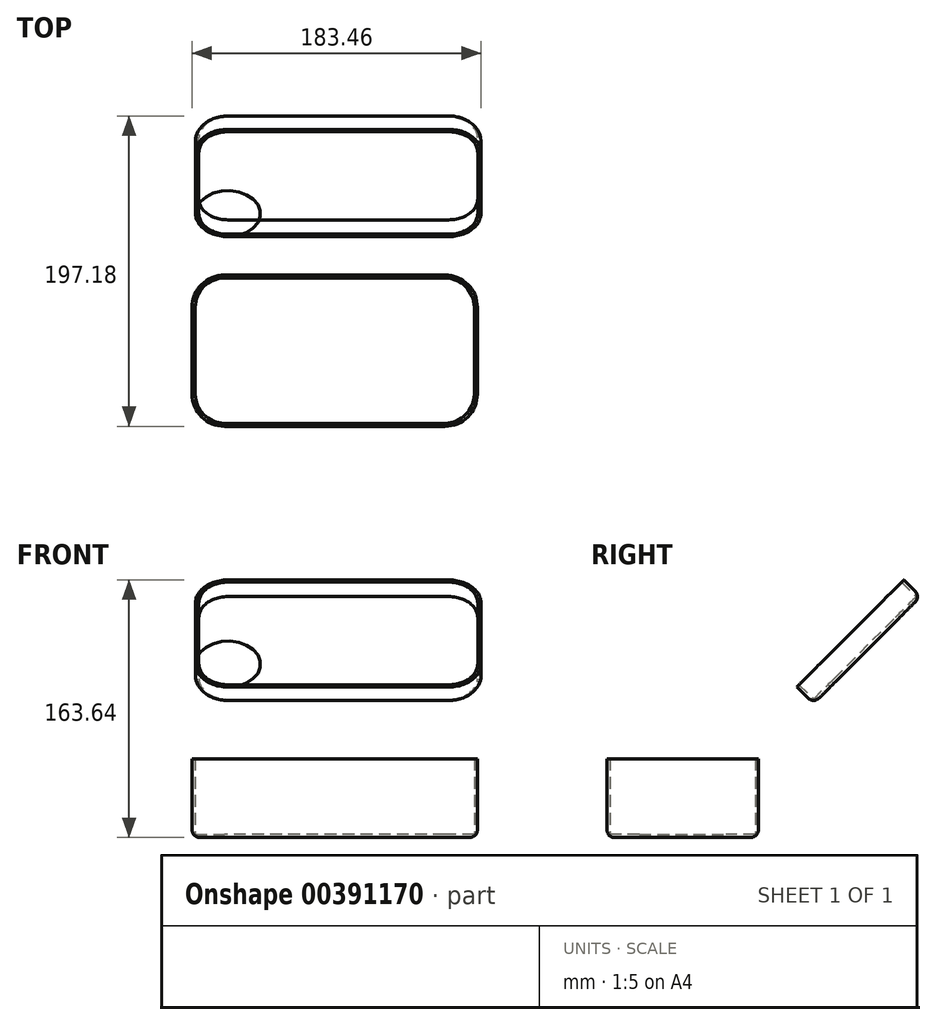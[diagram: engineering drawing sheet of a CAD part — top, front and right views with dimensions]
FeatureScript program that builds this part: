
annotation { "Feature Type Name" : "Feature", "Feature Type Description" : "" }
export const myFeature = defineFeature(function(context is Context, id is Id, definition is map)
    precondition{}
    {
        {
            var Q0;
            Q0=qCreatedBy(makeId("Top.planeOp"),FACE);
            var sketch = newSketch(context, id + "F0", { "sketchPlane" : qUnion([Q0])});
            skPoint(sketch, "E0.middle", {"position": v(0, 0) * mm});
            skLineSegment(sketch, "E1", {"start": v(-70.02, -46.05) * mm, "end": v(69.98, -46.05) * mm});
            skLineSegment(sketch, "E2", {"start": v(-88.63, -27.45) * mm, "end": v(-88.63, 27.55) * mm});
            skLineSegment(sketch, "E3", {"start": v(-90.63, 27.55) * mm, "end": v(-90.63, -27.45) * mm});
            skLineSegment(sketch, "E4", {"start": v(69.98, 46.16) * mm, "end": v(-70.02, 46.16) * mm});
            skLineSegment(sketch, "E5", {"start": v(-70.02, 48.16) * mm, "end": v(69.98, 48.16) * mm});
            skLineSegment(sketch, "E6", {"start": v(69.98, -48.05) * mm, "end": v(-70.02, -48.05) * mm});
            skArc(sketch, "E7", {"start": v(-90.63, 27.55) * mm, "mid": v(-84.6, 42.13) * mm, "end": v(-70.02, 48.16) * mm});
            skArc(sketch, "E8", {"start": v(-88.63, 27.55) * mm, "mid": v(-83.18, 40.71) * mm, "end": v(-70.02, 46.16) * mm});
            skArc(sketch, "E9", {"start": v(-70.02, -46.05) * mm, "mid": v(-83.18, -40.6) * mm, "end": v(-88.63, -27.45) * mm});
            skArc(sketch, "E10", {"start": v(-70.02, -48.05) * mm, "mid": v(-84.6, -42.02) * mm, "end": v(-90.63, -27.45) * mm});
            skLineSegment(sketch, "E11", {"start": v(90.59, 27.55) * mm, "end": v(90.59, -27.45) * mm});
            skArc(sketch, "E12", {"start": v(69.98, -46.05) * mm, "mid": v(83.14, -40.6) * mm, "end": v(88.59, -27.45) * mm});
            skArc(sketch, "E13", {"start": v(69.98, -48.05) * mm, "mid": v(84.55, -42.02) * mm, "end": v(90.59, -27.45) * mm});
            skLineSegment(sketch, "E14", {"start": v(88.59, 27.55) * mm, "end": v(88.59, -27.45) * mm});
            skArc(sketch, "E15", {"start": v(69.98, 46.16) * mm, "mid": v(83.14, 40.71) * mm, "end": v(88.59, 27.55) * mm});
            skArc(sketch, "E16", {"start": v(69.98, 48.16) * mm, "mid": v(84.55, 42.13) * mm, "end": v(90.59, 27.55) * mm});
            skSolve(sketch);
        }
        {
            var Q0;
            Q0=makeQuery(id+"F0.imprint","IMPRINT",FACE,{"disambiguationData":[TD([[makeQuery(id+"F0.imprint","IMPRINT",EDGE,{"derivedFrom":sQuery(id+"F0.wireOp",EDGE,"E1")}),-1.0]])]});
            extrude(context, id + "F1", {"entities" : qUnion([Q0]), "depth" : 50 * mm, "offsetDistance" : 25 * mm});
        }
        {
            var Q0;
            Q0=makeQuery(id+"F0.imprint","IMPRINT",FACE,{"disambiguationData":[TD([[makeQuery(id+"F0.imprint","IMPRINT",EDGE,{"derivedFrom":sQuery(id+"F0.wireOp",EDGE,"E1")}),1.0]])]});
            extrude(context, id + "F2", {"entities" : qUnion([Q0]), "operationType" : NewBodyOperationType.ADD, "depth" : 2 * mm});
        }
        {
            var Q0;
            Q0=makeQuery(id+"F1.opExtrude","CAP_EDGE",EDGE,{"disambiguationData":[OSD([sQuery(id+"F0.wireOp",EDGE,"7YGl0E8S-z3QK-v5Gx-pKp4-3rU6JJv4Ufol")])],"isStart":false});
            var Q1;
            Q1=makeQuery(id+"F1.opExtrude","CAP_EDGE",EDGE,{"disambiguationData":[OSD([sQuery(id+"F0.wireOp",EDGE,"E5")])],"isStart":false});
            cPlane(context, id + "F3", {"entities" : qUnion([Q0, Q1]), "cplaneType" : CPlaneType.LINE_ANGLE, "offset" : 25 * mm, "angle" : 135 * degree, "width" : 150 * mm, "height" : 150 * mm});
        }
        {
            var Q0;
            Q0=qCreatedBy(id+"F3.planeOp",FACE);
            var sketch = newSketch(context, id + "F4", { "sketchPlane" : qUnion([Q0])});
            skPoint(sketch, "E17.middle", {"position": v(-40.76, 166.96) * mm});
            skLineSegment(sketch, "E18", {"start": v(-67.78, 120.91) * mm, "end": v(72.22, 120.91) * mm});
            skLineSegment(sketch, "E19", {"start": v(-86.38, 139.52) * mm, "end": v(-86.38, 194.52) * mm});
            skLineSegment(sketch, "E20", {"start": v(-88.38, 194.52) * mm, "end": v(-88.38, 139.52) * mm});
            skLineSegment(sketch, "E21", {"start": v(72.22, 213.12) * mm, "end": v(-67.78, 213.12) * mm});
            skLineSegment(sketch, "E22", {"start": v(-67.78, 215.12) * mm, "end": v(72.22, 215.12) * mm});
            skLineSegment(sketch, "E23", {"start": v(72.22, 118.91) * mm, "end": v(-67.78, 118.91) * mm});
            skArc(sketch, "E24", {"start": v(-88.38, 194.52) * mm, "mid": v(-82.35, 209.09) * mm, "end": v(-67.78, 215.12) * mm});
            skArc(sketch, "E25", {"start": v(-86.38, 194.52) * mm, "mid": v(-80.94, 207.68) * mm, "end": v(-67.78, 213.12) * mm});
            skArc(sketch, "E26", {"start": v(-67.78, 120.91) * mm, "mid": v(-80.94, 126.36) * mm, "end": v(-86.38, 139.52) * mm});
            skArc(sketch, "E27", {"start": v(-67.78, 118.91) * mm, "mid": v(-82.35, 124.95) * mm, "end": v(-88.38, 139.52) * mm});
            skLineSegment(sketch, "E28", {"start": v(92.83, 194.52) * mm, "end": v(92.83, 139.52) * mm});
            skArc(sketch, "E29", {"start": v(72.22, 120.91) * mm, "mid": v(85.38, 126.36) * mm, "end": v(90.83, 139.52) * mm});
            skArc(sketch, "E30", {"start": v(72.22, 118.91) * mm, "mid": v(86.8, 124.95) * mm, "end": v(92.83, 139.52) * mm});
            skLineSegment(sketch, "E31", {"start": v(90.83, 194.52) * mm, "end": v(90.83, 139.52) * mm});
            skArc(sketch, "E32", {"start": v(72.22, 213.12) * mm, "mid": v(85.38, 207.68) * mm, "end": v(90.83, 194.52) * mm});
            skArc(sketch, "E33", {"start": v(72.22, 215.12) * mm, "mid": v(86.8, 209.09) * mm, "end": v(92.83, 194.52) * mm});
            skSolve(sketch);
        }
        {
            var Q0;
            Q0=makeQuery(id+"F4.imprint","IMPRINT",FACE,{"disambiguationData":[TD([[makeQuery(id+"F4.imprint","IMPRINT",EDGE,{"derivedFrom":sQuery(id+"F4.wireOp",EDGE,"E18")}),1.0]])]});
            extrude(context, id + "F5", {"entities" : qUnion([Q0]), "depth" : 2 * mm});
        }
        {
            var Q0;
            Q0=makeQuery(id+"F4.imprint","IMPRINT",FACE,{"disambiguationData":[TD([[makeQuery(id+"F4.imprint","IMPRINT",EDGE,{"derivedFrom":sQuery(id+"F4.wireOp",EDGE,"E18")}),-1.0]])]});
            extrude(context, id + "F6", {"entities" : qUnion([Q0]), "operationType" : NewBodyOperationType.ADD, "depth" : 15 * mm});
        }
        {
            var Q0;
            Q0=qCreatedBy(id+"F3.planeOp",FACE);
            var Q1;
            Q1=sQuery(id+"F4.wireOp",EDGE,"17cc7110-3d28-42bb-a2f8-b5e2e5a205e5");
            var Q2;
            Q2=sQuery(id+"F4.wireOp",EDGE,"E23");
            cPlane(context, id + "F7", {"entities" : qUnion([Q0, Q1, Q2]), "cplaneType" : CPlaneType.LINE_ANGLE, "offset" : 25 * mm, "angle" : 90 * degree, "width" : 150 * mm, "height" : 150 * mm});
        }
        {
            var Q0;
            Q0=qCreatedBy(id+"F7.planeOp",FACE);
            var sketch = newSketch(context, id + "F8", { "sketchPlane" : qUnion([Q0])});
            skLineSegment(sketch, "E34.bottom", {"start": v(-10, 0.7) * mm, "end": v(10, 0.7) * mm});
            skLineSegment(sketch, "E34.top", {"start": v(-10, -1.79) * mm, "end": v(10, -1.79) * mm});
            skLineSegment(sketch, "E34.left", {"start": v(-10, 0.7) * mm, "end": v(-10, -1.79) * mm});
            skLineSegment(sketch, "E34.right", {"start": v(10, 0.7) * mm, "end": v(10, -1.79) * mm});
            skSolve(sketch);
        }
        {
            var Q0;
            Q0=makeQuery(id+"F8.imprint","IMPRINT",FACE,{"disambiguationData":[TD([[makeQuery(id+"F8.imprint","IMPRINT",EDGE,{"derivedFrom":sQuery(id+"F8.wireOp",EDGE,"E34.bottom")}),-1.0]])]});
            extrude(context, id + "F9", {"entities" : qUnion([Q0]), "operationType" : NewBodyOperationType.REMOVE, "oppositeDirection" : true, "depth" : 2 * mm});
        }
        {
            var Q0;
            Q0=makeQuery(id+"F6.opExtrude","CAP_EDGE",EDGE,{"disambiguationData":[OSD([sQuery(id+"F4.wireOp",EDGE,"58a90a01-879d-4707-bce8-959e014baea4")])],"isStart":true});
            var Q1;
            Q1=makeQuery(id+"F6.opExtrude","CAP_EDGE",EDGE,{"disambiguationData":[OSD([sQuery(id+"F4.wireOp",EDGE,"daecf3bf-a768-478a-b0be-f2bc64202d3d")])],"isStart":true});
            var Q2;
            Q2=makeQuery(id+"F6.opExtrude","CAP_EDGE",EDGE,{"disambiguationData":[OSD([sQuery(id+"F4.wireOp",EDGE,"5c28383e-6da9-4aa2-90a1-f83498bbe82e")])],"isStart":true});
            var Q3;
            Q3=makeQuery(id+"F6.opExtrude","CAP_EDGE",EDGE,{"disambiguationData":[OSD([sQuery(id+"F4.wireOp",EDGE,"d15f32d5-d9fe-447c-bee9-bebc5e684c33")])],"isStart":true});
            var Q4;
            Q4=makeQuery(id+"F6.opExtrude","CAP_EDGE",EDGE,{"disambiguationData":[OSD([sQuery(id+"F4.wireOp",EDGE,"17cc7110-3d28-42bb-a2f8-b5e2e5a205e5")])],"isStart":true});
            var Q5;
            Q5=makeQuery(id+"F6.opExtrude","CAP_EDGE",EDGE,{"disambiguationData":[OSD([sQuery(id+"F4.wireOp",EDGE,"c21d17e3-76b5-43e2-9bd4-ec7192ce76eb")])],"isStart":true});
            var Q6;
            Q6=makeQuery(id+"F6.opExtrude","CAP_EDGE",EDGE,{"disambiguationData":[OSD([sQuery(id+"F4.wireOp",EDGE,"8e1f4fb9-b622-4703-8bfe-e7020bb5fb1f")])],"isStart":true});
            var Q7;
            Q7=makeQuery(id+"F6.opExtrude","CAP_EDGE",EDGE,{"disambiguationData":[OSD([sQuery(id+"F4.wireOp",EDGE,"a3704540-73f4-401e-ad48-26373cc9a367")])],"isStart":true});
            var Q8;
            {var subQ0=sQuery(id+"F4.wireOp",EDGE,"E32");var subQ1=sQuery(id+"F4.wireOp",EDGE,"E31");var subQ2=sQuery(id+"F4.wireOp",EDGE,"E29");var subQ3=sQuery(id+"F4.wireOp",EDGE,"E26");var subQ4=sQuery(id+"F4.wireOp",EDGE,"E25");var subQ5=sQuery(id+"F4.wireOp",EDGE,"E21");var subQ6=sQuery(id+"F4.wireOp",EDGE,"E19");var subQ7=sQuery(id+"F4.wireOp",EDGE,"E18");Q8=makeQuery(id+"F6.boolean.opBoolean","MERGE",FACE,{"derivedFrom":[makeQuery(id+"F5.opExtrude","CAP_FACE",FACE,{"disambiguationData":[OSD([subQ7,subQ6,subQ5,subQ4,subQ3,subQ2,subQ1,subQ0])],"isStart":true}),makeQuery(id+"F6.opExtrude","CAP_FACE",FACE,{"disambiguationData":[OSD([subQ7,subQ6,sQuery(id+"F4.wireOp",EDGE,"E20"),subQ5,sQuery(id+"F4.wireOp",EDGE,"E22"),sQuery(id+"F4.wireOp",EDGE,"E23"),sQuery(id+"F4.wireOp",EDGE,"E24"),subQ4,subQ3,sQuery(id+"F4.wireOp",EDGE,"E27"),sQuery(id+"F4.wireOp",EDGE,"E28"),subQ2,sQuery(id+"F4.wireOp",EDGE,"E30"),subQ1,subQ0,sQuery(id+"F4.wireOp",EDGE,"E33")])],"isStart":true})]});}
            fillet(context, id + "F10", {"entities" : qUnion([Q0, Q1, Q2, Q3, Q4, Q5, Q6, Q7, Q8]), "radius" : 5 * mm, "tangentPropagation" : true, "allowEdgeOverflow" : false});
        }
        {
            var Q0;
            {var subQ0=sQuery(id+"F0.wireOp",EDGE,"E15");var subQ1=sQuery(id+"F0.wireOp",EDGE,"E14");var subQ2=sQuery(id+"F0.wireOp",EDGE,"E12");var subQ3=sQuery(id+"F0.wireOp",EDGE,"E9");var subQ4=sQuery(id+"F0.wireOp",EDGE,"E8");var subQ5=sQuery(id+"F0.wireOp",EDGE,"E4");var subQ6=sQuery(id+"F0.wireOp",EDGE,"E2");var subQ7=sQuery(id+"F0.wireOp",EDGE,"E1");Q0=makeQuery(id+"F2.boolean.opBoolean","MERGE",FACE,{"derivedFrom":[makeQuery(id+"F1.opExtrude","CAP_FACE",FACE,{"disambiguationData":[OSD([subQ7,subQ6,sQuery(id+"F0.wireOp",EDGE,"E3"),subQ5,sQuery(id+"F0.wireOp",EDGE,"E5"),sQuery(id+"F0.wireOp",EDGE,"E6"),sQuery(id+"F0.wireOp",EDGE,"E7"),subQ4,subQ3,sQuery(id+"F0.wireOp",EDGE,"E10"),sQuery(id+"F0.wireOp",EDGE,"E11"),subQ2,sQuery(id+"F0.wireOp",EDGE,"E13"),subQ1,subQ0,sQuery(id+"F0.wireOp",EDGE,"E16")])],"isStart":true}),makeQuery(id+"F2.opExtrude","CAP_FACE",FACE,{"disambiguationData":[OSD([subQ7,subQ6,subQ5,subQ4,subQ3,subQ2,subQ1,subQ0])],"isStart":true})]});}
            fillet(context, id + "F11", {"entities" : qUnion([Q0]), "radius" : 5 * mm, "tangentPropagation" : true, "allowEdgeOverflow" : false});
        }
    });
